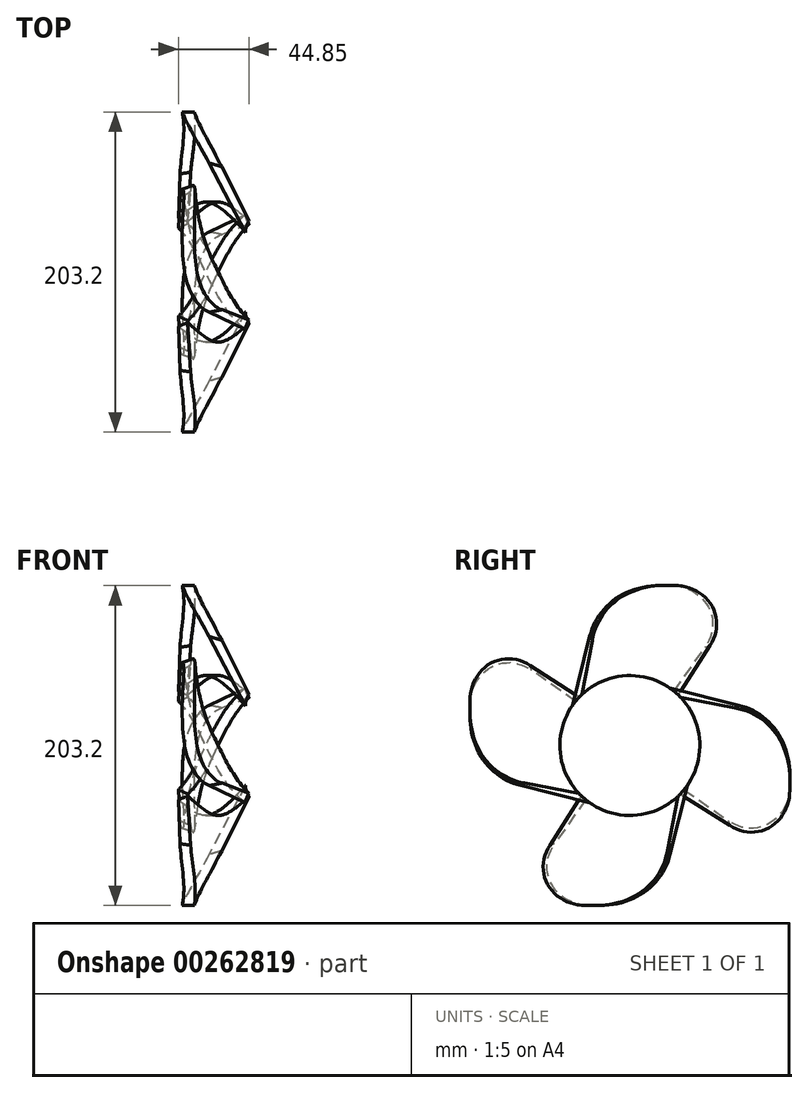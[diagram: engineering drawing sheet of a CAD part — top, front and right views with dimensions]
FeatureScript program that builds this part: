
annotation { "Feature Type Name" : "Feature", "Feature Type Description" : "" }
export const myFeature = defineFeature(function(context is Context, id is Id, definition is map)
    precondition{}
    {
        {
            var Q0;
            Q0=qCreatedBy(makeId("Front.planeOp"),FACE);
            var sketch = newSketch(context, id + "F0", { "sketchPlane" : qUnion([Q0])});
            skLineSegment(sketch, "E0", {"start": v(-37.76, 10.27) * mm, "end": v(19.39, -36.5) * mm});
            skLineSegment(sketch, "E1", {"start": v(19.39, -36.5) * mm, "end": v(14.13, -42.92) * mm});
            skLineSegment(sketch, "E2", {"start": v(14.13, -42.92) * mm, "end": v(-43, 3.84) * mm});
            skLineSegment(sketch, "E3", {"start": v(-43, 3.84) * mm, "end": v(-37.76, 10.27) * mm});
            skSolve(sketch);
        }
        {
            var Q0;
            Q0=qCreatedBy(makeId("Front.planeOp"),FACE);
            cPlane(context, id + "F1", {"entities" : qUnion([Q0]), "cplaneType" : CPlaneType.OFFSET, "offset" : 101.6 * mm, "width" : 152.4 * mm, "height" : 152.4 * mm});
        }
        {
            var Q0;
            Q0=qCreatedBy(id+"F1.planeOp",FACE);
            var sketch = newSketch(context, id + "F2", { "sketchPlane" : qUnion([Q0])});
            skLineSegment(sketch, "E4.bottom", {"start": v(-39.25, 75.34) * mm, "end": v(-31.61, 75.34) * mm});
            skLineSegment(sketch, "E4.top", {"start": v(-39.25, -17.36) * mm, "end": v(-31.61, -17.36) * mm});
            skLineSegment(sketch, "E4.left", {"start": v(-39.25, 75.34) * mm, "end": v(-39.25, -17.36) * mm});
            skLineSegment(sketch, "E4.right", {"start": v(-31.61, 75.34) * mm, "end": v(-31.61, -17.36) * mm});
            skSolve(sketch);
        }
        {
            var Q0;
            Q0=makeQuery(id+"F0.imprint","IMPRINT",FACE,{"disambiguationData":[TD([[makeQuery(id+"F0.imprint","IMPRINT",EDGE,{"derivedFrom":sQuery(id+"F0.wireOp",EDGE,"E0")}),-1.0]])]});
            var Q1;
            Q1=makeQuery(id+"F2.imprint","IMPRINT",FACE,{"disambiguationData":[TD([[makeQuery(id+"F2.imprint","IMPRINT",EDGE,{"derivedFrom":sQuery(id+"F2.wireOp",EDGE,"E4.bottom")}),-1.0]])]});
            loft(context, id + "F3", {"sheetProfilesArray" : [{ "sheetProfileEntities" : qUnion([Q0]) }, { "sheetProfileEntities" : qUnion([Q1]) }]});
        }
        {
            var Q0;
            Q0=makeQuery(id+"F3.opLoft","MID_CAP_EDGE",EDGE,{"disambiguationData":[OSD([sQuery(id+"F2.wireOp",EDGE,"E4.bottom"),sQuery(id+"F2.wireOp",EDGE,"E4.left"),sQuery(id+"F2.wireOp",EDGE,"E4.right")])],"capPos":1.0});
            fillet(context, id + "F4", {"entities" : qUnion([Q0]), "radius" : 25.4 * mm, "tangentPropagation" : true, "allowEdgeOverflow" : false});
        }
        {
            var Q0;
            Q0=makeQuery(id+"F3.opLoft","MID_CAP_EDGE",EDGE,{"disambiguationData":[OSD([sQuery(id+"F2.wireOp",EDGE,"E4.top"),sQuery(id+"F2.wireOp",EDGE,"E4.left"),sQuery(id+"F2.wireOp",EDGE,"E4.right")])],"capPos":1.0});
            fillet(context, id + "F5", {"entities" : qUnion([Q0]), "radius" : 50.8 * mm, "tangentPropagation" : true, "allowEdgeOverflow" : false});
        }
        {
            var Q0;
            Q0=qCreatedBy(makeId("Right.planeOp"),FACE);
            var sketch = newSketch(context, id + "F6", { "sketchPlane" : qUnion([Q0])});
            skCircle(sketch, "E5", {"center": v(0, 0) * mm, "radius": 44.44 * mm});
            skSolve(sketch);
        }
        {
            var Q0;
            Q0=makeQuery(id+"F6.imprint","IMPRINT",FACE,{"disambiguationData":[TD([[makeQuery(id+"F6.imprint","IMPRINT",EDGE,{"derivedFrom":sQuery(id+"F6.wireOp",EDGE,"E5")}),1.0]])]});
            extrude(context, id + "F7", {"entities" : qUnion([Q0]), "depth" : 25.4 * mm, "hasSecondDirection" : true, "secondDirectionOppositeDirection" : true, "secondDirectionDepth" : 50.8 * mm});
        }
        {
            var Q0;
            Q0=makeQuery(id+"F3.opLoft","SWEPT_BODY",BODY,{"disambiguationData":[OSD([makeQuery(id+"F0.imprint","IMPRINT",FACE,{"disambiguationData":[TD([[makeQuery(id+"F0.imprint","IMPRINT",EDGE,{"derivedFrom":sQuery(id+"F0.wireOp",EDGE,"E0")}),-1.0]])]}),makeQuery(id+"F2.imprint","IMPRINT",FACE,{"disambiguationData":[TD([[makeQuery(id+"F2.imprint","IMPRINT",EDGE,{"derivedFrom":sQuery(id+"F2.wireOp",EDGE,"E4.bottom")}),-1.0]])]})])]});
            var Q1;
            Q1=makeQuery(id+"F7.opExtrude","SWEPT_FACE",FACE,{"disambiguationData":[OSD([sQuery(id+"F6.wireOp",EDGE,"E5")])]});
            circularPattern(context, id + "F8", {"entities" : qUnion([Q0]), "axis" : qUnion([Q1]), "angle" : 360 * degree, "instanceCount" : 4, "equalSpace" : true});
        }
        {
            var Q0;
            Q0=makeQuery(id+"F7.opExtrude","CAP_FACE",FACE,{"disambiguationData":[OSD([sQuery(id+"F6.wireOp",EDGE,"E5")])],"isStart":false});
            var sketch = newSketch(context, id + "F9", { "sketchPlane" : qUnion([Q0])});
            skCircle(sketch, "E6", {"center": v(0, 0) * mm, "radius": 33.58 * mm});
            skSolve(sketch);
        }
        {
            var Q0;
            Q0=makeQuery(id+"F9.imprint","IMPRINT",FACE,{"disambiguationData":[TD([[makeQuery(id+"F9.imprint","IMPRINT",EDGE,{"derivedFrom":sQuery(id+"F9.wireOp",EDGE,"E6")}),1.0]])]});
            extrude(context, id + "F10", {"entities" : qUnion([Q0]), "operationType" : NewBodyOperationType.REMOVE, "oppositeDirection" : true, "depth" : 25.4 * mm});
        }
        {
            var Q0;
            Q0=makeQuery(id+"F7.opExtrude","CAP_FACE",FACE,{"disambiguationData":[OSD([sQuery(id+"F6.wireOp",EDGE,"E5")])],"isStart":false});
            var sketch = newSketch(context, id + "F11", { "sketchPlane" : qUnion([Q0])});
            skCircle(sketch, "E7.0", {"center": v(0, 0) * mm, "radius": 44.44 * mm});
            skSolve(sketch);
        }
        {
            var Q0;
            Q0=qSketchRegion(id+"F11",true);
            extrude(context, id + "F12", {"entities" : qUnion([Q0]), "operationType" : NewBodyOperationType.REMOVE, "oppositeDirection" : true, "depth" : 92.2 * mm});
        }
    });
